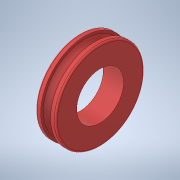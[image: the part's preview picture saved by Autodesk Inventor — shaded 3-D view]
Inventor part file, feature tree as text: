
AUTODESK INVENTOR PART (.ipt)
format: ipt  version: 2022.3 (Build 263350000, 350)  size: 171,520 bytes
history: native  units: in
note: dims shown in document units (in); Inventor stores cm internally (conversion verified against a paired STEP export)
features: sketch x4, extrude x3, revolve x1, fillet x1
ambient origin geometry x8: Origin, YZ Plane, XZ Plane, XY Plane, X Axis, Y Axis, Z Axis, Center Point
bodies: Solid1 (feature_tree)
feature tree (9):
  revolve  "Revolution1"  [1 undecoded]
  extrude  "Extrusion1"  TaperAngle=90.0deg  [1 undecoded]
  extrude  "Extrusion2"  Depth=0.125in TaperAngle=0.0deg
  extrude  "Extrusion3"  Depth=0.125in TaperAngle=0.0deg
  fillet  "Fillet1"  Radius=1.125in
  sketch  "Sketch1"  dims[d0=0.135in d1=1.0in]
  sketch  "Sketch2"  dims[d2=0.235in d3=90.0deg]
  sketch  "Sketch3"  dims[d4=2.125in d5=0.125in d6=0.0in]
  sketch  "Sketch4"  dims[d7=2.125in d8=0.125in d9=0.0in d10=1.125in d11=0.0in d12=0.0in d13=0.0375in]
note: 2 required parameter values undecoded (feature->parameter linkage not recoverable at this tier; creation-order binding heuristic only, values carry confidence <= 0.55)